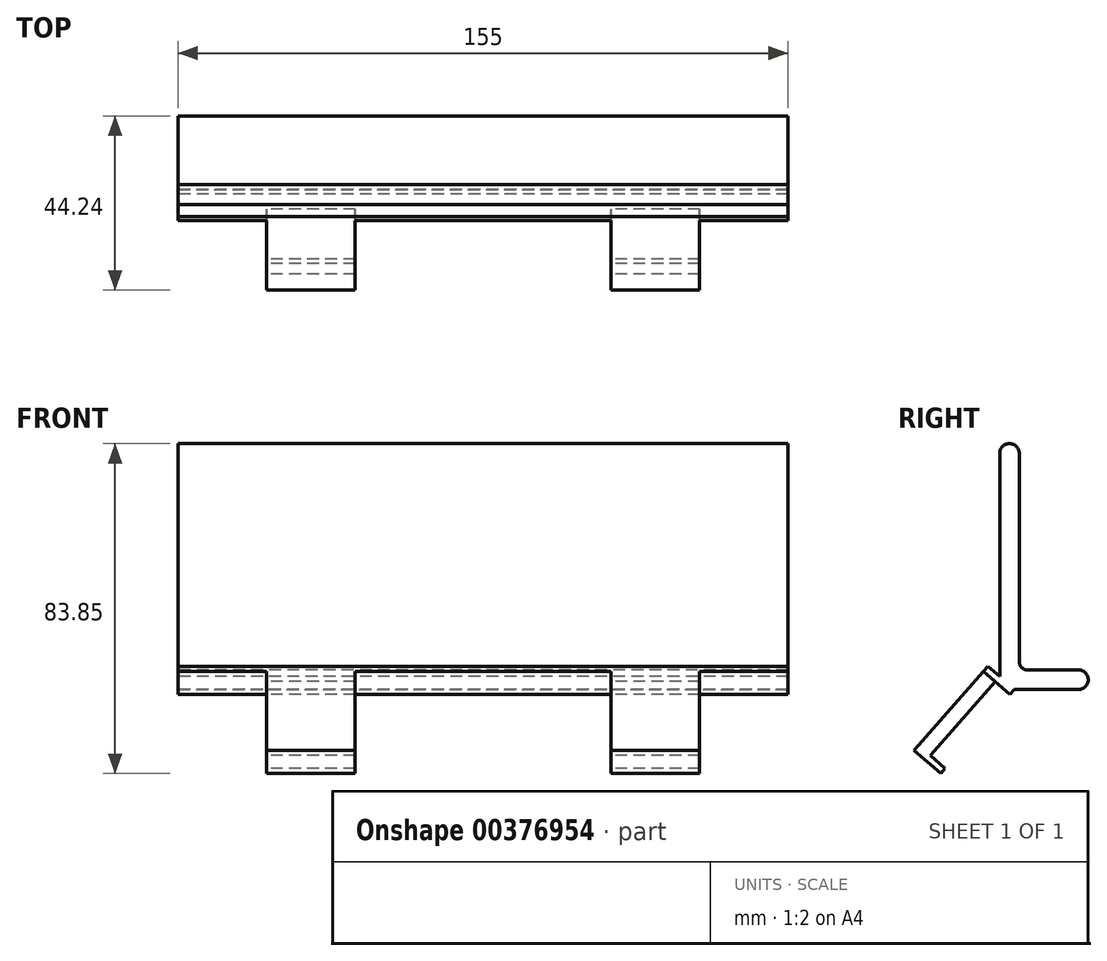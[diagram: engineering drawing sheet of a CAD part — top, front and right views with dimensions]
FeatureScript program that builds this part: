
annotation { "Feature Type Name" : "Feature", "Feature Type Description" : "" }
export const myFeature = defineFeature(function(context is Context, id is Id, definition is map)
    precondition{}
    {
        {
            var Q0;
            Q0=qCreatedBy(makeId("Right.planeOp"),FACE);
            var sketch = newSketch(context, id + "F0", { "sketchPlane" : qUnion([Q0])});
            skLineSegment(sketch, "E0", {"start": v(-30.4, 39.52) * mm, "end": v(-30.4, -18.48) * mm});
            skLineSegment(sketch, "E1", {"start": v(-28.4, -20.48) * mm, "end": v(-10.4, -20.48) * mm});
            skLineSegment(sketch, "E2", {"start": v(-10.4, -20.48) * mm, "end": v(-10.4, -15.48) * mm});
            skLineSegment(sketch, "E3", {"start": v(-10.4, -15.48) * mm, "end": v(-10.4, -22.36) * mm});
            skLineSegment(sketch, "E4", {"start": v(-10.4, -15.48) * mm, "end": v(-23.4, -15.48) * mm});
            skLineSegment(sketch, "E5", {"start": v(-25.4, -13.48) * mm, "end": v(-25.4, 39.52) * mm});
            skLineSegment(sketch, "E6", {"start": v(-25.4, 39.52) * mm, "end": v(-30.4, 39.52) * mm});
            skArc(sketch, "E7", {"start": v(-25.4, 39.52) * mm, "mid": v(-27.9, 42.02) * mm, "end": v(-30.4, 39.52) * mm});
            skArc(sketch, "E8", {"start": v(-10.4, -20.48) * mm, "mid": v(-7.9, -17.98) * mm, "end": v(-10.4, -15.48) * mm});
            skPoint(sketch, "E9.visualSharp", {"position": v(-30.4, -20.48) * mm});
            skArc(sketch, "E9.filletArc", {"start": v(-30.4, -18.48) * mm, "mid": v(-29.81, -19.9) * mm, "end": v(-28.4, -20.48) * mm});
            skPoint(sketch, "E10.visualSharp", {"position": v(-25.4, -15.48) * mm});
            skArc(sketch, "E10.filletArc", {"start": v(-25.4, -13.48) * mm, "mid": v(-24.81, -14.9) * mm, "end": v(-23.4, -15.48) * mm});
            skSolve(sketch);
        }
        {
            var Q0;
            Q0 = qSketchRegion(id + "F0", true);
            extrude(context, id + "F1", {"entities" : qUnion([Q0]), "depth" : 155 * mm});
        }
        {
            var Q0;
            Q0=qCreatedBy(makeId("Right.planeOp"),FACE);
            var sketch = newSketch(context, id + "F2", { "sketchPlane" : qUnion([Q0])});
            skLineSegment(sketch, "E11", {"start": v(-33.4, -14.54) * mm, "end": v(-34.53, -15.82) * mm});
            skLineSegment(sketch, "E12", {"start": v(-34.53, -15.82) * mm, "end": v(-27.76, -21.76) * mm});
            skLineSegment(sketch, "E13", {"start": v(-27.76, -21.76) * mm, "end": v(-26.64, -20.48) * mm});
            skLineSegment(sketch, "E14", {"start": v(-26.64, -20.48) * mm, "end": v(-33.4, -14.54) * mm});
            skSolve(sketch);
        }
        {
            var Q0;
            Q0 = qSketchRegion(id + "F2", true);
            extrude(context, id + "F3", {"entities" : qUnion([Q0]), "operationType" : NewBodyOperationType.ADD, "depth" : 155 * mm});
        }
        {
            var Q0;
            Q0=qCreatedBy(makeId("Right.planeOp"),FACE);
            var sketch = newSketch(context, id + "F4", { "sketchPlane" : qUnion([Q0])});
            skLineSegment(sketch, "E15", {"start": v(-34.53, -15.82) * mm, "end": v(-51.02, -34.61) * mm});
            skLineSegment(sketch, "E16", {"start": v(-51.02, -34.61) * mm, "end": v(-48, -37.25) * mm});
            skLineSegment(sketch, "E17", {"start": v(-48, -37.25) * mm, "end": v(-31.52, -18.46) * mm});
            skLineSegment(sketch, "E18", {"start": v(-31.52, -18.46) * mm, "end": v(-34.53, -15.82) * mm});
            skSolve(sketch);
        }
        {
            var Q0;
            Q0=makeQuery(id+"F4.imprint","IMPRINT",FACE,{"disambiguationData":[TD([[makeQuery(id+"F4.imprint","IMPRINT",EDGE,{"derivedFrom":sQuery(id+"F4.wireOp",EDGE,"E15")}),1.0]])]});
            extrude(context, id + "F5", {"entities" : qUnion([Q0]), "operationType" : NewBodyOperationType.ADD, "depth" : 45 * mm, "hasSecondDirection" : true, "secondDirectionOppositeDirection" : false, "secondDirectionDepth" : 22.5 * mm});
        }
        {
            var Q0;
            Q0=makeQuery(id+"F4.imprint","IMPRINT",FACE,{"disambiguationData":[TD([[makeQuery(id+"F4.imprint","IMPRINT",EDGE,{"derivedFrom":sQuery(id+"F4.wireOp",EDGE,"E15")}),1.0]])]});
            extrude(context, id + "F6", {"entities" : qUnion([Q0]), "operationType" : NewBodyOperationType.ADD, "depth" : 132.5 * mm, "hasSecondDirection" : true, "secondDirectionOppositeDirection" : false, "secondDirectionDepth" : 110 * mm});
        }
        {
            var Q0;
            Q0=qCreatedBy(makeId("Right.planeOp"),FACE);
            var sketch = newSketch(context, id + "F7", { "sketchPlane" : qUnion([Q0])});
            skLineSegment(sketch, "E19", {"start": v(-52.14, -35.9) * mm, "end": v(-45.37, -41.83) * mm});
            skLineSegment(sketch, "E20", {"start": v(-45.37, -41.83) * mm, "end": v(-44.25, -40.55) * mm});
            skLineSegment(sketch, "E21", {"start": v(-44.25, -40.55) * mm, "end": v(-51.02, -34.61) * mm});
            skLineSegment(sketch, "E22", {"start": v(-51.02, -34.61) * mm, "end": v(-52.14, -35.9) * mm});
            skSolve(sketch);
        }
        {
            var Q0;
            Q0 = qSketchRegion(id + "F7", true);
            extrude(context, id + "F8", {"entities" : qUnion([Q0]), "operationType" : NewBodyOperationType.ADD, "depth" : 45 * mm, "hasSecondDirection" : true, "secondDirectionOppositeDirection" : false, "secondDirectionDepth" : 22.5 * mm});
        }
        {
            var Q0;
            Q0 = qSketchRegion(id + "F7", true);
            extrude(context, id + "F9", {"entities" : qUnion([Q0]), "operationType" : NewBodyOperationType.ADD, "depth" : 132.5 * mm, "hasSecondDirection" : true, "secondDirectionOppositeDirection" : false, "secondDirectionDepth" : 110 * mm});
        }
    });
